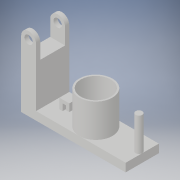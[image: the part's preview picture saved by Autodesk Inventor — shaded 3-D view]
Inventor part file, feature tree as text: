
AUTODESK INVENTOR PART (.ipt)
format: ipt  version: 2019 (Build 230136000, 136)  size: 182,272 bytes
history: native  units: in
note: dims shown in document units (in); Inventor stores cm internally (conversion verified against a paired STEP export)
features: sketch x7, extrude x6
ambient origin geometry x8: Origin, YZ Plane, XZ Plane, XY Plane, X Axis, Y Axis, Z Axis, Center Point
bodies: Solid1 (feature_tree)
feature tree (13):
  extrude  "Extrusion1"  Depth=0.1969in
  sketch  "Sketch2"  dims[d6=0.1772in d7=0.1969in]
  sketch  "Sketch6"  dims[d8=0.3543in d9=2.126in]
  extrude  "Extrusion5"  Depth=0.1969in
  sketch  "Sketch8"  dims[d13=0.2559in d14=0.7874in]
  extrude  "Extrusion6"  Depth=2.126in
  extrude  "Extrusion7"  Depth=0.7874in
  extrude  "Extrusion8"  Depth=0.7874in
  extrude  "Extrusion9"  Depth=0.3937in
  sketch  "Sketch1"  dims[d0=1.5748in d2=0.1969in]
  sketch  "Sketch7"  dims[d10=0.7874in d11=0.0in d12=0.1181in]
  sketch  "Sketch9"  dims[d16=1.0236in d19=0.3937in]
  sketch  "Sketch10"  dims[d20=0.1575in d21=0.3937in d22=0.5512in d40=0.5512in d41=0.5512in d42=0.5906in d43=0.5512in d44=0.0in d47=1.2795in d48=0.7874in d49=0.0in d50=0.7087in d51=0.9843in d52=0.0in d53=0.2362in d54=0.1575in d55=0.315in d56=0.2362in d57=0.2362in d58=0.0in d59=0.0787in d60=0.0787in d61=0.1575in d62=0.0591in d63=0.1575in d64=0.0in]
